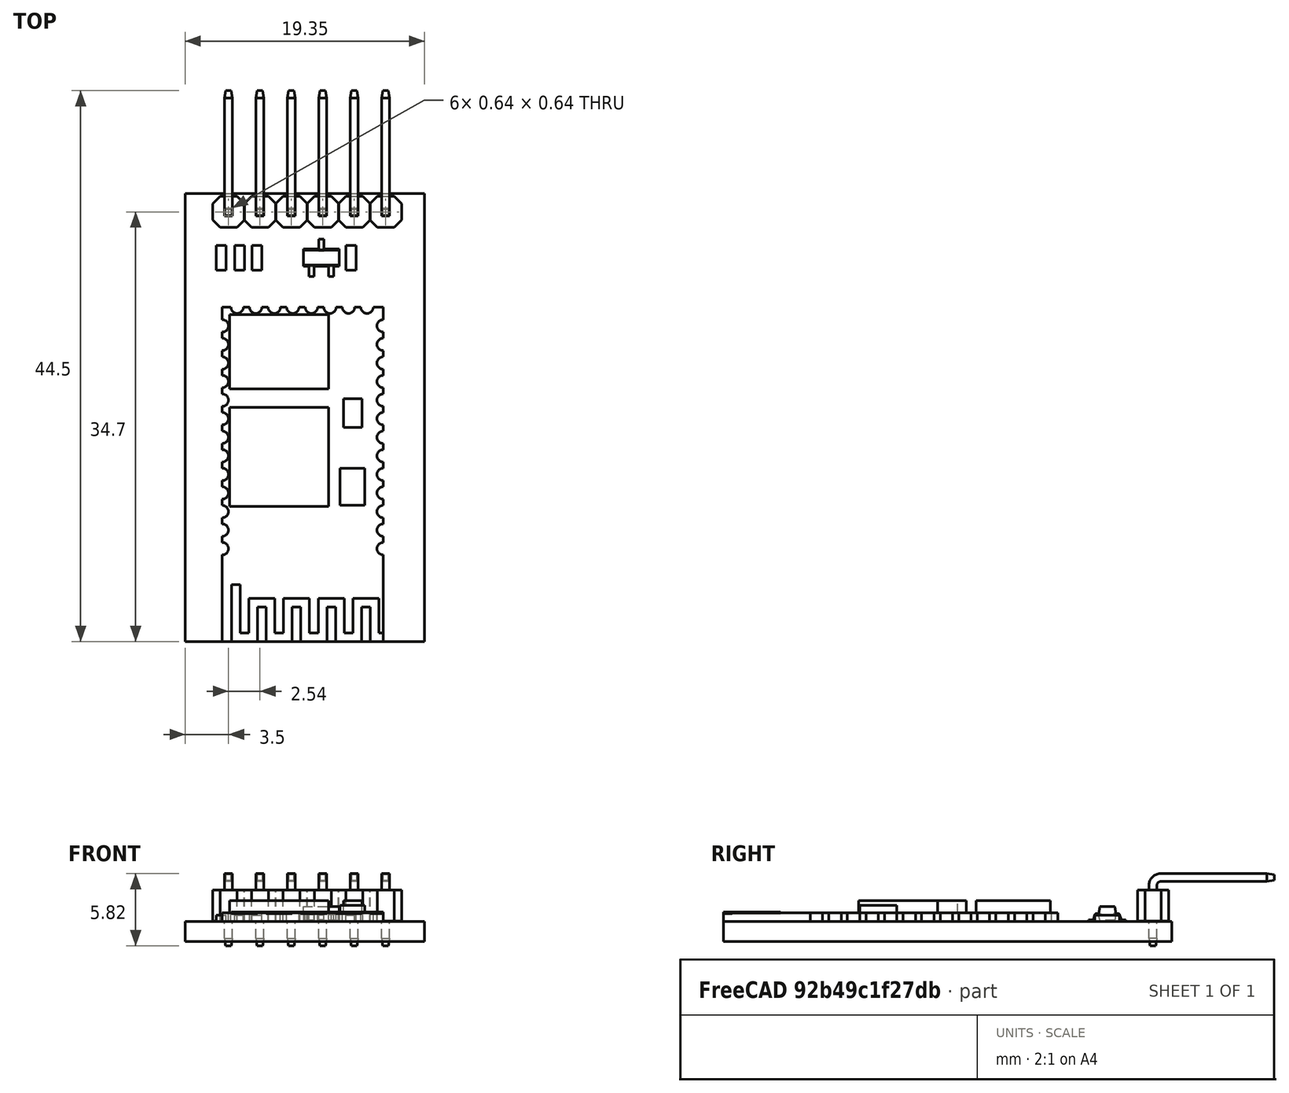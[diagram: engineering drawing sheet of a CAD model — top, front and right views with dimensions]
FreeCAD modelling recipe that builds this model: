
FCSTD DOCUMENT  (FreeCAD 0.14R3692 (Git))
Label: Bluetooth_HC05
License: CC-BY 3.0
LicenseURL: http://creativecommons.org/licenses/by/3.0/
objects: Part::Box×9, Part::Sweep×4, App::DocumentObjectGroup×2, Part::FeaturePython×1, Part::Cut×1, PartDesign::Pad×1
note: 17 computed .brp shape members not serialized (recipe doc carries the construction recipe); baked Part::Feature solids carry a one-line shape summary decoded from their .brp

FEATURE [Part::Box] Box  label="BaseBT"
  Height = 1.6
  Length = 19.35
  Width = 36.2
FEATURE [Part::FeaturePython] Array  label="Conector6PinesAng"  # Draft array (typed FeaturePython)
  Angle = 360
  ArrayType = 0
  Axis = (0,0,1)
  Center = (0,0,0)
  IntervalX = (1,0,0)
  IntervalY = (0,2.54,0)
  IntervalZ = (0,0,1)
  NumberPolar = 1
  NumberX = 1
  NumberY = 6
  NumberZ = 1
  Placement = pos=(3.5,34.7,-0.35) rot=(0,0,-1;1.5708rad)
FEATURE [Part::Cut] Cut
FEATURE [Part::Sweep] Sweep
  Frenet = false
  Placement = pos=(9.5,0,0) rot=(0,0,1;0rad)
  Solid = true
  Transition = 1
FEATURE [Part::Box] Box002  label="Cubo"
  Height = 1
  Length = 8
  Placement = pos=(3.6,20.4,2.3) rot=(0,0,1;0rad)
  Width = 6
FEATURE [Part::Box] Box003  label="Cubo001"
  Height = 1
  Length = 8
  Placement = pos=(3.6,10.9,2.3) rot=(0,0,1;0rad)
  Width = 8
FEATURE [Part::Box] Box004  label="Cubo002"
  Height = 0.6
  Length = 2
  Placement = pos=(12.5,11,2.3) rot=(0,0,1;0rad)
  Width = 3
FEATURE [Part::Box] Box005  label="Cubo003"
  Height = 1
  Length = 1.5
  Placement = pos=(12.8,17.3,2.3) rot=(0,0,1;0rad)
  Width = 2.3
FEATURE [App::DocumentObjectGroup] Grupo  label="HC-006"
  Group = -> [Cut,Sweep,Box002,Box003,Box004,Box005]
FEATURE [PartDesign::Pad] Pad
  Length = 2.9
  Length2 = 100
  Placement = pos=(9.55,31,2.2) rot=(0.57735,0.57735,0.57735;2.0944rad)
  Type = 0
FEATURE [Part::Sweep] Sweep001
  Frenet = false
  Placement = pos=(10.2,31,2.2) rot=(0,0,1;4.71239rad)
  Solid = true
  Transition = 1
FEATURE [Part::Sweep] Sweep002
  Frenet = false
  Placement = pos=(11.8,31,2.2) rot=(0,0,1;4.71239rad)
  Solid = true
  Transition = 1
FEATURE [Part::Sweep] Sweep003
  Frenet = false
  Placement = pos=(11,31,2.2) rot=(0,0,1;1.5708rad)
  Solid = true
  Transition = 1
FEATURE [App::DocumentObjectGroup] Grupo001  label="GR-SOT23"
  Group = -> [Pad,Sweep001,Sweep002,Sweep003]
FEATURE [Part::Box] Box006  label="R1"
  Height = 0.5
  Length = 0.8
  Placement = pos=(13,30,1.6) rot=(0,0,1;0rad)
  Width = 2
FEATURE [Part::Box] Box007  label="R002"
  Height = 0.5
  Length = 0.8
  Placement = pos=(2.5,30,1.6) rot=(0,0,1;0rad)
  Width = 2
FEATURE [Part::Box] Box008  label="R003"
  Height = 0.5
  Length = 0.8
  Placement = pos=(4,30,1.6) rot=(0,0,1;0rad)
  Width = 2
FEATURE [Part::Box] Box009  label="R004"
  Height = 0.5
  Length = 0.8
  Placement = pos=(5.4,30,1.6) rot=(0,0,1;0rad)
  Width = 2
